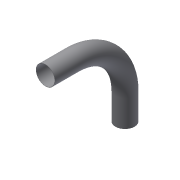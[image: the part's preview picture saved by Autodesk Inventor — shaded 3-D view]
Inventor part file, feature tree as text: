
AUTODESK INVENTOR PART (.ipt)
format: ipt  version: 2016 (Build 200138000, 138)  size: 129,024 bytes
history: native  units: in
note: dims shown in document units (in); Inventor stores cm internally (conversion verified against a paired STEP export)
features: sketch x4, extrude x2, plane x1, sweep x1
ambient origin geometry x8: Origin, YZ Plane, XZ Plane, XY Plane, X Axis, Y Axis, Z Axis, Center Point
bodies: Solid1 (feature_tree)
feature tree (8):
  extrude  "Extrusion1"  Depth=0.0906in
  sketch  "Sketch4"  dims[d2=6.0in d3=0.0in d7=12.0in]
  plane  "Work Plane4"
  sweep  "Sweep1"
  extrude  "Extrusion2"  Depth=6.0in TaperAngle=0.0deg
  sketch  "Sketch1"  dims[d0=4.3307in d1=0.0906in]
  sketch  "Sketch8"  dims[d9=0.0in d10=6.0in d11=0.0in]
  sketch  "Sketch9"  dims[d12=0.0in]
